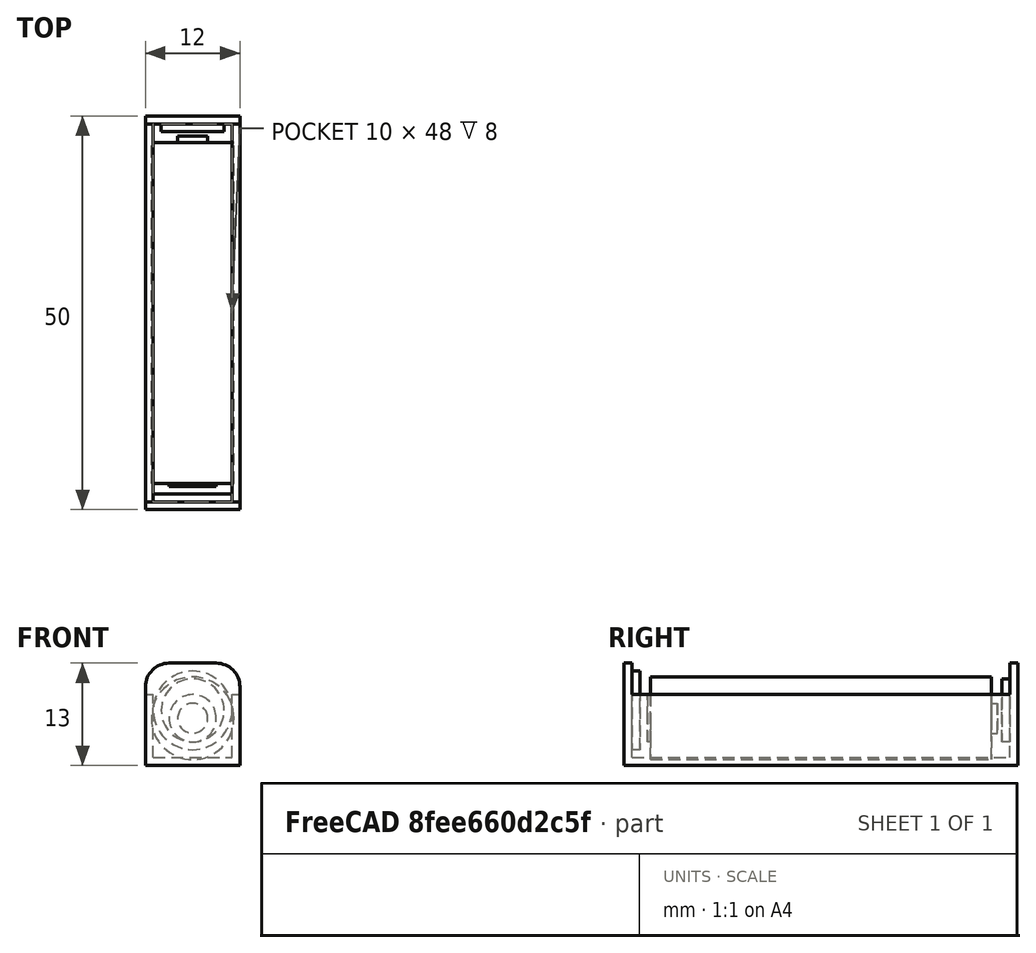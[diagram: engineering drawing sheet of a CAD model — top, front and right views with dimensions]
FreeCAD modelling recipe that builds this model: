
FCSTD DOCUMENT  (FreeCAD 0.16R6712 (Git))
Label: Holder+AAA
License: All rights reserved
LicenseURL: http://en.wikipedia.org/wiki/All_rights_reserved
objects: Part::Cylinder×5, Part::Compound×3, Part::Box×3, Part::Cut×2, Part::Fillet×1
note: 14 computed .brp shape members not serialized (recipe doc carries the construction recipe); baked Part::Feature solids carry a one-line shape summary decoded from their .brp

FEATURE [Part::Cylinder] Cylinder
  Angle = 360
  Height = 43.3
  Placement = pos=(0,-21.65,0) rot=(-1,0,0;1.5708rad)
  Radius = 5.25
FEATURE [Part::Cylinder] Cylinder001  label="Plus"
  Angle = 360
  Height = 0.8
  Placement = pos=(0,21.65,0) rot=(-1,0,0;1.5708rad)
  Radius = 1.9
FEATURE [Part::Cylinder] Cylinder002  label="Minus"
  Angle = 360
  Height = 0.4
  Placement = pos=(0,-21.65,0) rot=(1,0,0;1.5708rad)
  Radius = 3
FEATURE [Part::Compound] Compound
  Links = -> [Cylinder,Cylinder001,Cylinder002]
FEATURE [Part::Box] Box  label="Kostka"
  Height = 13
  Length = 12
  Width = 50
FEATURE [Part::Box] Box001  label="Kostka001"
  Height = 12
  Length = 10
  Placement = pos=(1,1,1) rot=(0,0,1;0rad)
  Width = 48
FEATURE [Part::Cut] Cut
  Base = -> Box
  Tool = -> Box001
FEATURE [Part::Cylinder] Cylinder003  label="Minus001"
  Angle = 360
  Height = 1
  Placement = pos=(6,2,7) rot=(1,0,0;1.5708rad)
  Radius = 5
FEATURE [Part::Cylinder] Cylinder004  label="Plus001"
  Angle = 360
  Height = 1
  Placement = pos=(6,49,7) rot=(1,0,0;1.5708rad)
  Radius = 4
FEATURE [Part::Box] Box002  label="Kostka002"
  Height = 4
  Length = 12
  Placement = pos=(0,1,9) rot=(0,0,1;0rad)
  Width = 48
FEATURE [Part::Cut] Cut001
  Base = -> Cut
  Tool = -> Box002
FEATURE [Part::Fillet] Fillet
  Base = -> Cut001
  Edges = 4 edges r=3: [Edge1,Edge5,Edge12,Edge21]
FEATURE [Part::Compound] Compound001
  Links = -> [Cylinder003,Cylinder004,Fillet]
  Placement = pos=(-6,-25,-6) rot=(0,0,1;0rad)
FEATURE [Part::Compound] Compound002
  Links = -> [Compound,Compound001]
